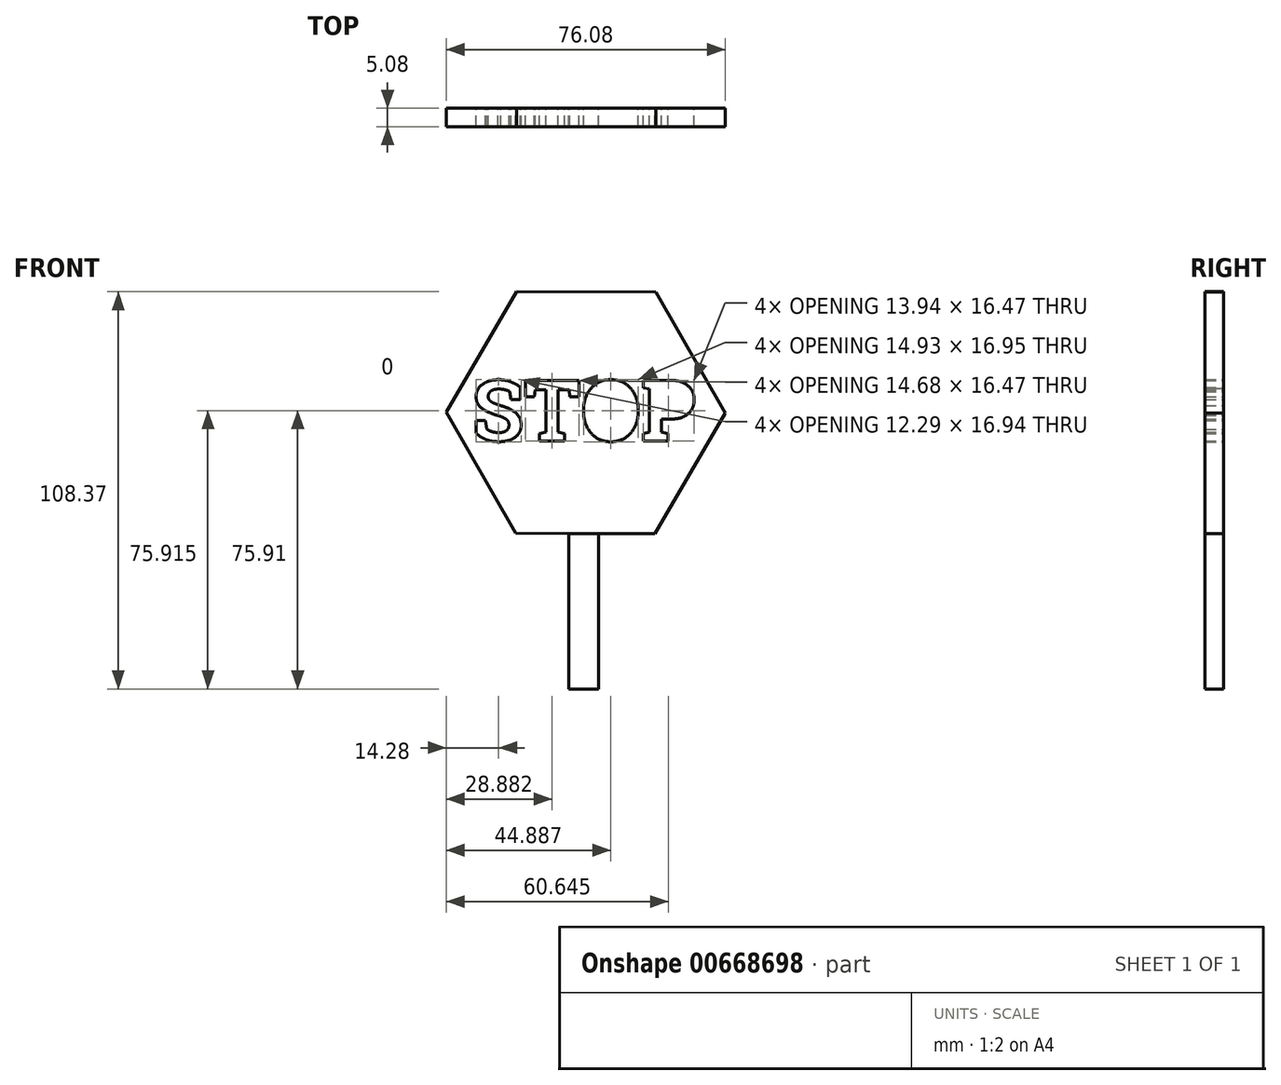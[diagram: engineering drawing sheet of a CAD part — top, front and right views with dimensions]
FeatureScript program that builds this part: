
annotation { "Feature Type Name" : "Feature", "Feature Type Description" : "" }
export const myFeature = defineFeature(function(context is Context, id is Id, definition is map)
    precondition{}
    {
        {
            var Q0;
            Q0=qCreatedBy(makeId("Front.planeOp"),FACE);
            var sketch = newSketch(context, id + "F0", { "sketchPlane" : qUnion([Q0])});
            skPoint(sketch, "E0.middle", {"position": v(0, 0) * mm});
            skText(sketch, "E1", { "text": "STOP", "fontName": "RobotoSlab-Bold.ttf"});
            skCircle(sketch, "E2.cCircle", {"center": v(0, 0) * mm, "radius": 38.04 * mm, "construction": true});
            skLineSegment(sketch, "E2.0", {"start": v(-19.14, -32.87) * mm, "end": v(-38.04, 0.14) * mm});
            skLineSegment(sketch, "E2.1", {"start": v(-38.04, 0.14) * mm, "end": v(-18.9, 33) * mm});
            skLineSegment(sketch, "E2.2", {"start": v(-18.9, 33) * mm, "end": v(19.14, 32.87) * mm});
            skLineSegment(sketch, "E2.3", {"start": v(19.14, 32.87) * mm, "end": v(38.04, -0.14) * mm});
            skLineSegment(sketch, "E2.4", {"start": v(38.04, -0.14) * mm, "end": v(18.9, -33) * mm});
            skLineSegment(sketch, "E2.5", {"start": v(18.9, -33) * mm, "end": v(-19.14, -32.87) * mm});
            skLineSegment(sketch, "E3.bottom", {"start": v(-4.64, -32.92) * mm, "end": v(3.5, -32.92) * mm});
            skLineSegment(sketch, "E3.top", {"start": v(-4.64, -75.36) * mm, "end": v(3.5, -75.36) * mm});
            skLineSegment(sketch, "E3.left", {"start": v(-4.64, -32.92) * mm, "end": v(-4.64, -75.36) * mm});
            skLineSegment(sketch, "E3.right", {"start": v(3.5, -32.92) * mm, "end": v(3.5, -75.36) * mm});
            const initialGuessF0  = {"E1": [-0.031, -0.00768, 1, 0, 0.01668]};
            skSetInitialGuess(sketch, initialGuessF0);
            skSolve(sketch);
        }
        {
            var Q0;
            Q0=makeQuery(id+"F0.imprint","IMPRINT",FACE,{"disambiguationData":[TD([[makeQuery(id+"F0.imprint","IMPRINT",EDGE,{"derivedFrom":sQuery(id+"F0.wireOp",EDGE,"E1.sketch_text.stroke-0")}),1.0]])]});
            var Q1;
            {var subQ4=sQuery(id+"F0.wireOp",EDGE,"E3.top");Q1=makeQuery(id+"F0.imprint","IMPRINT",FACE,{"disambiguationData":[TD([[makeQuery(id+"F0.imprint","IMPRINT",EDGE,{"derivedFrom":subQ4}),1.0]])]});}
            extrude(context, id + "F1", {"entities" : qUnion([Q0, Q1]), "endBound" : BoundingType.SYMMETRIC, "depth" : 5.08 * mm, "offsetDistance" : 25.4 * mm});
        }
    });
